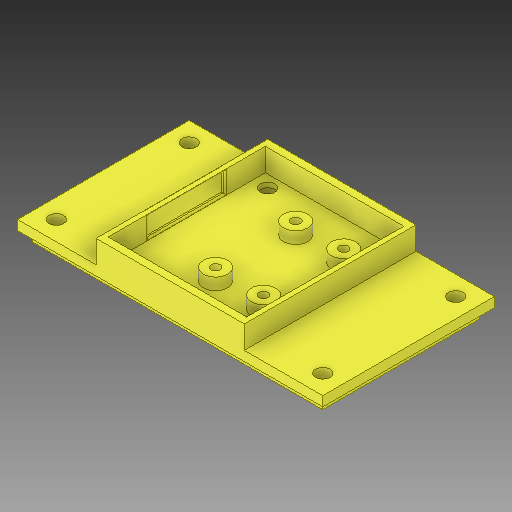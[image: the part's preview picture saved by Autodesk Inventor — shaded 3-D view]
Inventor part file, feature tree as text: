
AUTODESK INVENTOR PART (.ipt)
format: ipt  version: 2019.3 (Build 233278000, 278)  size: 258,560 bytes
history: native  units: in
note: dims shown in document units (in); Inventor stores cm internally (conversion verified against a paired STEP export)
features: sketch x8, other x6, extrude x5, reference x4, hole x3, fillet x1, projected_geometry x1
ambient origin geometry x8: Origin, YZ Plane, XZ Plane, XY Plane, X Axis, Y Axis, Z Axis, Center Point
bodies: Solid1 (feature_tree)
feature tree (28):
  extrude  "ExtrusionForTopOfCase"  Depth=1.7717in
  extrude  "ExtrusionForBottomRidge"  Depth=0.075in
  sketch  "Sketch8"  dims[d7=0.075in d8=0.1in d9=0.0in]
  extrude  "Extrusion7"  Depth=0.1in TaperAngle=0.0deg
  extrude  "Extrusion8"  Depth=0.125in
  fillet  "Fillet1"  Radius=0.125in
  hole  "Hole7"  [1 undecoded]
  hole  "Hole12"  [1 undecoded]
  extrude  "Extrusion10"  Depth=0.2362in TaperAngle=0.0deg
  hole  "Hole14"  [1 undecoded]
  sketch  "Sketch1"  dims[d0=3.1496in d1=1.7717in]
  sketch  "Sketch2"  dims[d2=0.1in d3=0.0in d6=0.075in]
  sketch  "Sketch11"  dims[d39=0.125in d40=0.125in d41=0.125in]
  sketch  "Sketch13"  dims[d42=0.125in d57=0.81in]
  sketch  "Sketch21"  dims[d58=0.05in d59=0.05in]
  projected_geometry  "Projected Loop1"
  reference  "Reference1"
  reference  "Reference2"
  reference  "Reference3"
  reference  "Reference4"
  sketch  "Sketch22"  dims[d60=2.34in d61=0.2362in d62=0.0in]
  sketch  "Sketch24"  dims[d70=0.1969in d71=0.7874in d72=1.0in d73=0.0in d74=0.0167in d75=0.15in d76=0.75in d77=0.172in d78=0.25in d79=0.5635in d80=1.0in d81=0.8108in d123=0.151in d124=0.75in d125=0.191in d126=0.15in d127=0.5635in d128=1.0in d129=0.8108in d130=1.0835in d131=0.4724in d132=0.4953in d133=0.8268in d134=0.4953in d135=0.8268in d136=0.25in d137=0.122in d138=0.0in d146=0.096in d147=0.75in d148=0.1285in d149=0.157in d150=0.5635in d151=1.0in d152=0.8108in]
  other  "PiZeroAndCameraCases.iam"
  other  "Bolted Connection:7"
  other  "Unbrako UNC Hex Socket Button Cap - Inch 6 x 3/4:4"
  other  "Unbrako UNC Hex Socket Button Cap - Inch 6 x 3/4:1"
  other  "Unbrako UNC Hex Socket Button Cap - Inch 6 x 3/4:2"
  other  "Unbrako UNC Hex Socket Button Cap - Inch 6 x 3/4:3"
note: 3 required parameter values undecoded (feature->parameter linkage not recoverable at this tier; creation-order binding heuristic only, values carry confidence <= 0.55)
